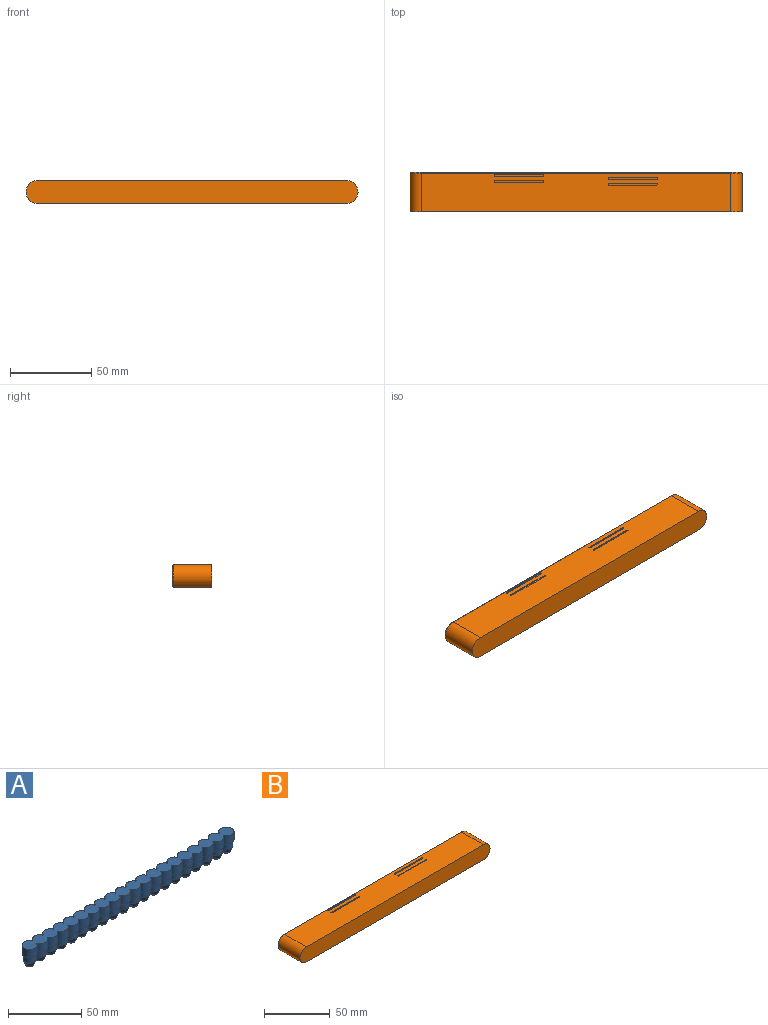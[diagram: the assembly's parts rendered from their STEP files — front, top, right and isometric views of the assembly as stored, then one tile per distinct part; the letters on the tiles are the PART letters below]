
ASSEMBLY  parts=2 mates=1
PART A: 158 faces, bbox 200.4x10.4x17 mm
  f0: cylinder r=5.2mm len=10.4mm, axis (0,0,1), area 198.4mm2, adj f66,f67,f76,f157
  f1: cylinder r=5.2mm len=9.51mm, axis (0,0,1), area 84.1mm2, adj f65,f66,f76,f157
  f2: cylinder r=5.2mm len=9.51mm, axis (0,0,1), area 84.1mm2, adj f64,f65,f76,f157
  f3: cylinder r=5.2mm len=9.51mm, axis (0,0,1), area 84.1mm2, adj f63,f64,f76,f157
  f4: cylinder r=5.2mm len=9.51mm, axis (0,0,1), area 84.1mm2, adj f62,f63,f76,f157
  f5: cylinder r=5.2mm len=9.51mm, axis (0,0,1), area 84.1mm2, adj f61,f62,f76,f157
  f6: cylinder r=5.2mm len=9.51mm, axis (0,0,1), area 84.1mm2, adj f60,f61,f76,f157
  f7: cylinder r=5.2mm len=9.51mm, axis (0,0,1), area 84.1mm2, adj f59,f60,f76,f157
  f8: cylinder r=5.2mm len=9.51mm, axis (0,0,1), area 84.1mm2, adj f58,f59,f76,f157
  f9: cylinder r=5.2mm len=9.51mm, axis (0,0,1), area 84.1mm2, adj f57,f58,f76,f157
  f10: cylinder r=5.2mm len=9.51mm, axis (0,0,1), area 84.1mm2, adj f56,f57,f76,f157
  f11: cylinder r=5.2mm len=9.51mm, axis (0,0,1), area 84.1mm2, adj f55,f56,f76,f157
  f12: cylinder r=5.2mm len=9.51mm, axis (0,0,1), area 84.1mm2, adj f54,f55,f76,f157
  f13: cylinder r=5.2mm len=9.51mm, axis (0,0,1), area 84.1mm2, adj f53,f54,f76,f157
  f14: cylinder r=5.2mm len=9.51mm, axis (0,0,1), area 84.1mm2, adj f52,f53,f76,f157
  f15: cylinder r=5.2mm len=9.51mm, axis (0,0,1), area 84.1mm2, adj f51,f52,f76,f157
  f16: cylinder r=5.2mm len=9.51mm, axis (0,0,1), area 84.1mm2, adj f50,f51,f76,f157
  f17: cylinder r=5.2mm len=9.51mm, axis (0,0,1), area 84.1mm2, adj f49,f50,f76,f157
  f18: cylinder r=5.2mm len=9.51mm, axis (0,0,1), area 84.1mm2, adj f48,f49,f76,f157
  f19: cylinder r=5.2mm len=10.4mm, axis (0,0,1), area 198.4mm2, adj f47,f48,f76,f157
  f20: cylinder r=5.2mm len=9.51mm, axis (0,0,1), area 84.1mm2, adj f39,f75,f76,f157
  f21: cylinder r=5.2mm len=9.51mm, axis (0,0,1), area 84.1mm2, adj f74,f75,f76,f157
  f22: cylinder r=5.2mm len=9.51mm, axis (0,0,1), area 84.1mm2, adj f73,f74,f76,f157
  f23: cylinder r=5.2mm len=9.51mm, axis (0,0,1), area 84.1mm2, adj f72,f73,f76,f157
  f24: cylinder r=5.2mm len=9.51mm, axis (0,0,1), area 84.1mm2, adj f71,f72,f76,f157
  f25: cylinder r=5.2mm len=9.51mm, axis (0,0,1), area 84.1mm2, adj f70,f71,f76,f157
  f26: cylinder r=5.2mm len=9.51mm, axis (0,0,1), area 84.1mm2, adj f69,f70,f76,f157
  f27: cylinder r=5.2mm len=9.51mm, axis (0,0,1), area 84.1mm2, adj f68,f69,f76,f157
  f28: cylinder r=5.2mm len=9.51mm, axis (0,0,1), area 84.1mm2, adj f67,f68,f76,f157
  f29: cylinder r=5.2mm len=9.51mm, axis (0,0,1), area 84.1mm2, adj f46,f47,f76,f157
  f30: cylinder r=5.2mm len=9.51mm, axis (0,0,1), area 84.1mm2, adj f45,f46,f76,f157
  f31: cylinder r=5.2mm len=9.51mm, axis (0,0,1), area 84.1mm2, adj f44,f45,f76,f157
  f32: cylinder r=5.2mm len=9.51mm, axis (0,0,1), area 84.1mm2, adj f43,f44,f76,f157
  f33: cylinder r=5.2mm len=9.51mm, axis (0,0,1), area 84.1mm2, adj f42,f43,f76,f157
  f34: cylinder r=5.2mm len=9.51mm, axis (0,0,1), area 84.1mm2, adj f41,f42,f76,f157
  f35: cylinder r=5.2mm len=9.51mm, axis (0,0,1), area 84.1mm2, adj f40,f41,f76,f157
  f36: cylinder r=5.2mm len=9.51mm, axis (0,0,1), area 84.1mm2, adj f38,f40,f76,f157
  f37: cylinder r=5.2mm len=9.51mm, axis (0,0,1), area 84.1mm2, adj f38,f39,f76,f157
  f38: plane 7x0.49mm, normal (0,-1,0), area 3.4mm2, adj f36,f37,f76,f157
  f39: plane 7x0.49mm, normal (0,-1,0), area 3.4mm2, adj f20,f37,f76,f157
  f40: plane 7x0.49mm, normal (0,-1,0), area 3.4mm2, adj f35,f36,f76,f157
  f41: plane 7x0.49mm, normal (0,-1,0), area 3.4mm2, adj f34,f35,f76,f157
  f42: plane 7x0.49mm, normal (0,-1,0), area 3.4mm2, adj f33,f34,f76,f157
  f43: plane 7x0.49mm, normal (0,-1,0), area 3.4mm2, adj f32,f33,f76,f157
  f44: plane 7x0.49mm, normal (0,-1,0), area 3.4mm2, adj f31,f32,f76,f157
  f45: plane 7x0.49mm, normal (0,-1,0), area 3.4mm2, adj f30,f31,f76,f157
  f46: plane 7x0.49mm, normal (0,-1,0), area 3.4mm2, adj f29,f30,f76,f157
  f47: plane 7x0.49mm, normal (0,-1,0), area 3.4mm2, adj f19,f29,f76,f157
  f48: plane 7x0.49mm, normal (0,1,0), area 3.4mm2, adj f18,f19,f76,f157
  f49: plane 7x0.49mm, normal (0,1,0), area 3.4mm2, adj f17,f18,f76,f157
  f50: plane 7x0.49mm, normal (0,1,0), area 3.4mm2, adj f16,f17,f76,f157
  f51: plane 7x0.49mm, normal (0,1,0), area 3.4mm2, adj f15,f16,f76,f157
  f52: plane 7x0.49mm, normal (0,1,0), area 3.4mm2, adj f14,f15,f76,f157
  f53: plane 7x0.49mm, normal (0,1,0), area 3.4mm2, adj f13,f14,f76,f157
  f54: plane 7x0.49mm, normal (0,1,0), area 3.4mm2, adj f12,f13,f76,f157
  f55: plane 7x0.49mm, normal (0,1,0), area 3.4mm2, adj f11,f12,f76,f157
  f56: plane 7x0.49mm, normal (0,1,0), area 3.4mm2, adj f10,f11,f76,f157
  f57: plane 7x0.49mm, normal (0,1,0), area 3.4mm2, adj f9,f10,f76,f157
  f58: plane 7x0.49mm, normal (0,1,0), area 3.4mm2, adj f8,f9,f76,f157
  f59: plane 7x0.49mm, normal (0,1,0), area 3.4mm2, adj f7,f8,f76,f157
  f60: plane 7x0.49mm, normal (0,1,0), area 3.4mm2, adj f6,f7,f76,f157
  f61: plane 7x0.49mm, normal (0,1,0), area 3.4mm2, adj f5,f6,f76,f157
  f62: plane 7x0.49mm, normal (0,1,0), area 3.4mm2, adj f4,f5,f76,f157
  f63: plane 7x0.49mm, normal (0,1,0), area 3.4mm2, adj f3,f4,f76,f157
  f64: plane 7x0.49mm, normal (0,1,0), area 3.4mm2, adj f2,f3,f76,f157
  f65: plane 7x0.49mm, normal (0,1,0), area 3.4mm2, adj f1,f2,f76,f157
  f66: plane 7x0.49mm, normal (0,1,0), area 3.4mm2, adj f0,f1,f76,f157
  f67: plane 7x0.49mm, normal (0,-1,0), area 3.4mm2, adj f0,f28,f76,f157
  f68: plane 7x0.49mm, normal (0,-1,0), area 3.4mm2, adj f27,f28,f76,f157
  f69: plane 7x0.49mm, normal (0,-1,0), area 3.4mm2, adj f26,f27,f76,f157
  f70: plane 7x0.49mm, normal (0,-1,0), area 3.4mm2, adj f25,f26,f76,f157
  f71: plane 7x0.49mm, normal (0,-1,0), area 3.4mm2, adj f24,f25,f76,f157
  f72: plane 7x0.49mm, normal (0,-1,0), area 3.4mm2, adj f23,f24,f76,f157
  f73: plane 7x0.49mm, normal (0,-1,0), area 3.4mm2, adj f22,f23,f76,f157
  f74: plane 7x0.49mm, normal (0,-1,0), area 3.4mm2, adj f21,f22,f76,f157
  f75: plane 7x0.49mm, normal (0,-1,0), area 3.4mm2, adj f20,f21,f76,f157
  f76: plane 200.4x10.4mm, normal (0,0,-1), area 417.9mm2, adj f0,f1,f2,f3,f4,f5,f6,f7
  f77: cylinder r=4.5mm len=9mm, axis (0,0,1), area 141.4mm2, adj f76,f136
  f78: plane 2.29x2.29mm, normal (0,0,-1), area 4.1mm2, adj f137
  f79: cylinder r=4.5mm len=9mm, axis (0,0,1), area 141.4mm2, adj f76,f135
  f80: plane 2.29x2.29mm, normal (0,0,-1), area 4.1mm2, adj f138
  f81: cylinder r=4.5mm len=9mm, axis (0,0,1), area 141.4mm2, adj f76,f134
  f82: plane 2.29x2.29mm, normal (0,0,-1), area 4.1mm2, adj f139
  f83: cylinder r=4.5mm len=9mm, axis (0,0,1), area 141.4mm2, adj f76,f133
  f84: plane 2.29x2.29mm, normal (0,0,-1), area 4.1mm2, adj f140
  f85: cylinder r=4.5mm len=9mm, axis (0,0,1), area 141.4mm2, adj f76,f132
  f86: plane 2.29x2.29mm, normal (0,0,-1), area 4.1mm2, adj f141
  f87: cylinder r=4.5mm len=9mm, axis (0,0,1), area 141.4mm2, adj f76,f131
  f88: plane 2.29x2.29mm, normal (0,0,-1), area 4.1mm2, adj f142
  f89: cylinder r=4.5mm len=9mm, axis (0,0,1), area 141.4mm2, adj f76,f130
  f90: plane 2.29x2.29mm, normal (0,0,-1), area 4.1mm2, adj f143
  f91: cylinder r=4.5mm len=9mm, axis (0,0,1), area 141.4mm2, adj f76,f129
  f92: plane 2.29x2.29mm, normal (0,0,-1), area 4.1mm2, adj f144
  f93: cylinder r=4.5mm len=9mm, axis (0,0,1), area 141.4mm2, adj f76,f128
  f94: plane 2.29x2.29mm, normal (0,0,-1), area 4.1mm2, adj f145
  f95: cylinder r=4.5mm len=9mm, axis (0,0,1), area 141.4mm2, adj f76,f127
  f96: plane 2.29x2.29mm, normal (0,0,-1), area 4.1mm2, adj f146
  f97: cylinder r=4.5mm len=9mm, axis (0,0,1), area 141.4mm2, adj f76,f126
  f98: plane 2.29x2.29mm, normal (0,0,-1), area 4.1mm2, adj f147
  f99: cylinder r=4.5mm len=9mm, axis (0,0,1), area 141.4mm2, adj f76,f125
  f100: plane 2.29x2.29mm, normal (0,0,-1), area 4.1mm2, adj f148
  f101: cylinder r=4.5mm len=9mm, axis (0,0,1), area 141.4mm2, adj f76,f124
  f102: plane 2.29x2.29mm, normal (0,0,-1), area 4.1mm2, adj f149
  f103: cylinder r=4.5mm len=9mm, axis (0,0,1), area 141.4mm2, adj f76,f123
  f104: plane 2.29x2.29mm, normal (0,0,-1), area 4.1mm2, adj f150
  f105: cylinder r=4.5mm len=9mm, axis (0,0,1), area 141.4mm2, adj f76,f122
  f106: plane 2.29x2.29mm, normal (0,0,-1), area 4.1mm2, adj f151
  f107: cylinder r=4.5mm len=9mm, axis (0,0,1), area 141.4mm2, adj f76,f121
  f108: plane 2.29x2.29mm, normal (0,0,-1), area 4.1mm2, adj f152
  f109: cylinder r=4.5mm len=9mm, axis (0,0,1), area 141.4mm2, adj f76,f120
  f110: plane 2.29x2.29mm, normal (0,0,-1), area 4.1mm2, adj f153
  f111: cylinder r=4.5mm len=9mm, axis (0,0,1), area 141.4mm2, adj f76,f119
  f112: plane 2.29x2.29mm, normal (0,0,-1), area 4.1mm2, adj f154
  f113: cylinder r=4.5mm len=9mm, axis (0,0,1), area 141.4mm2, adj f76,f118
  f114: plane 2.29x2.29mm, normal (0,0,-1), area 4.1mm2, adj f155
  f115: cylinder r=4.5mm len=9mm, axis (0,0,1), area 141.4mm2, adj f76,f117
  f116: plane 2.29x2.29mm, normal (0,0,-1), area 4.1mm2, adj f156
  f117: cone r=2.5mm half-angle=21.8deg, axis (0,0,1), area 95mm2, adj f115,f156
  f118: cone r=2.5mm half-angle=21.8deg, axis (0,0,1), area 95mm2, adj f113,f155
  f119: cone r=2.5mm half-angle=21.8deg, axis (0,0,1), area 95mm2, adj f111,f154
  f120: cone r=2.5mm half-angle=21.8deg, axis (0,0,1), area 95mm2, adj f109,f153
  f121: cone r=2.5mm half-angle=21.8deg, axis (0,0,1), area 95mm2, adj f107,f152
  f122: cone r=2.5mm half-angle=21.8deg, axis (0,0,1), area 95mm2, adj f105,f151
  f123: cone r=2.5mm half-angle=21.8deg, axis (0,0,1), area 95mm2, adj f103,f150
  f124: cone r=2.5mm half-angle=21.8deg, axis (0,0,1), area 95mm2, adj f101,f149
  f125: cone r=2.5mm half-angle=21.8deg, axis (0,0,1), area 95mm2, adj f99,f148
  f126: cone r=2.5mm half-angle=21.8deg, axis (0,0,1), area 95mm2, adj f97,f147
  f127: cone r=2.5mm half-angle=21.8deg, axis (0,0,1), area 95mm2, adj f95,f146
  f128: cone r=2.5mm half-angle=21.8deg, axis (0,0,1), area 95mm2, adj f93,f145
  f129: cone r=2.5mm half-angle=21.8deg, axis (0,0,1), area 95mm2, adj f91,f144
  f130: cone r=2.5mm half-angle=21.8deg, axis (0,0,1), area 95mm2, adj f89,f143
  f131: cone r=2.5mm half-angle=21.8deg, axis (0,0,1), area 95mm2, adj f87,f142
  f132: cone r=2.5mm half-angle=21.8deg, axis (0,0,1), area 95mm2, adj f85,f141
  f133: cone r=2.5mm half-angle=21.8deg, axis (0,0,1), area 95mm2, adj f83,f140
  f134: cone r=2.5mm half-angle=21.8deg, axis (0,0,1), area 95mm2, adj f81,f139
  f135: cone r=2.5mm half-angle=21.8deg, axis (0,0,1), area 95mm2, adj f79,f138
  f136: cone r=2.5mm half-angle=21.8deg, axis (0,0,1), area 95mm2, adj f77,f137
  f137: torus R=1.15mm, axis (0,0,-1), area 32.9mm2, adj f78,f136
  f138: torus R=1.15mm, axis (0,0,-1), area 32.9mm2, adj f80,f135
  f139: torus R=1.15mm, axis (0,0,-1), area 32.9mm2, adj f82,f134
  f140: torus R=1.15mm, axis (0,0,-1), area 32.9mm2, adj f84,f133
  f141: torus R=1.15mm, axis (0,0,-1), area 32.9mm2, adj f86,f132
  f142: torus R=1.15mm, axis (0,0,-1), area 32.9mm2, adj f88,f131
  f143: torus R=1.15mm, axis (0,0,-1), area 32.9mm2, adj f90,f130
  f144: torus R=1.15mm, axis (0,0,-1), area 32.9mm2, adj f92,f129
  f145: torus R=1.15mm, axis (0,0,-1), area 32.9mm2, adj f94,f128
  f146: torus R=1.15mm, axis (0,0,-1), area 32.9mm2, adj f96,f127
  f147: torus R=1.15mm, axis (0,0,-1), area 32.9mm2, adj f98,f126
  f148: torus R=1.15mm, axis (0,0,-1), area 32.9mm2, adj f100,f125
  f149: torus R=1.15mm, axis (0,0,-1), area 32.9mm2, adj f102,f124
  f150: torus R=1.15mm, axis (0,0,-1), area 32.9mm2, adj f104,f123
  f151: torus R=1.15mm, axis (0,0,-1), area 32.9mm2, adj f106,f122
  f152: torus R=1.15mm, axis (0,0,-1), area 32.9mm2, adj f108,f121
  f153: torus R=1.15mm, axis (0,0,-1), area 32.9mm2, adj f110,f120
  f154: torus R=1.15mm, axis (0,0,-1), area 32.9mm2, adj f112,f119
  f155: torus R=1.15mm, axis (0,0,-1), area 32.9mm2, adj f114,f118
  f156: torus R=1.15mm, axis (0,0,-1), area 32.9mm2, adj f116,f117
  f157: plane 200.4x10.4mm, normal (0,0,1), area 1690.2mm2, adj f0,f1,f2,f3,f4,f5,f6,f7
PART B: 187 faces, bbox 204x24x14 mm
  f0: plane 29x0.5mm, normal (0,-1,0), area 14.5mm2, adj f2,f6,f179,f183
  f1: plane 29x0.5mm, normal (0,1,0), area 14.5mm2, adj f2,f6,f179,f183
  f2: plane 30x1mm, normal (0,0,1), area 29.8mm2, adj f0,f1,f179,f183
  f3: plane 29x0.5mm, normal (0,-1,0), area 14.5mm2, adj f5,f6,f181,f185
  f4: plane 29x0.5mm, normal (0,1,0), area 14.5mm2, adj f5,f6,f181,f185
  f5: plane 30x1mm, normal (0,0,1), area 29.8mm2, adj f3,f4,f181,f185
  f6: plane 190x23.5mm, normal (0,0,1), area 4345.9mm2, adj f0,f1,f3,f4,f127,f128,f129,f131
  f7: cylinder r=5.2mm len=10.4mm, axis (0,1,0), area 255.1mm2, adj f27,f46,f170,f171
  f8: cylinder r=5.2mm len=9.51mm, axis (0,1,0), area 108.1mm2, adj f27,f46,f169,f170
  f9: cylinder r=5.2mm len=9.51mm, axis (0,1,0), area 108.1mm2, adj f27,f46,f168,f169
  f10: cylinder r=5.2mm len=9.51mm, axis (0,1,0), area 108.1mm2, adj f27,f46,f167,f168
  f11: cylinder r=5.2mm len=9.51mm, axis (0,1,0), area 108.1mm2, adj f27,f46,f166,f167
  f12: cylinder r=5.2mm len=9.51mm, axis (0,1,0), area 108.1mm2, adj f27,f46,f165,f166
  f13: cylinder r=5.2mm len=9.51mm, axis (0,1,0), area 108.1mm2, adj f27,f46,f164,f165
  f14: cylinder r=5.2mm len=9.51mm, axis (0,1,0), area 108.1mm2, adj f27,f46,f163,f164
  f15: cylinder r=5.2mm len=9.51mm, axis (0,1,0), area 108.1mm2, adj f27,f46,f162,f163
  f16: cylinder r=5.2mm len=9.51mm, axis (0,1,0), area 108.1mm2, adj f27,f46,f161,f162
  f17: cylinder r=5.2mm len=9.51mm, axis (0,1,0), area 108.1mm2, adj f27,f46,f160,f161
  f18: cylinder r=5.2mm len=9.51mm, axis (0,1,0), area 108.1mm2, adj f27,f46,f159,f160
  f19: cylinder r=5.2mm len=9.51mm, axis (0,1,0), area 108.1mm2, adj f27,f46,f158,f159
  f20: cylinder r=5.2mm len=9.51mm, axis (0,1,0), area 108.1mm2, adj f27,f46,f157,f158
  f21: cylinder r=5.2mm len=9.51mm, axis (0,1,0), area 108.1mm2, adj f27,f46,f156,f157
  f22: cylinder r=5.2mm len=9.51mm, axis (0,1,0), area 108.1mm2, adj f27,f46,f155,f156
  f23: cylinder r=5.2mm len=9.51mm, axis (0,1,0), area 108.1mm2, adj f27,f46,f154,f155
  f24: cylinder r=5.2mm len=9.51mm, axis (0,1,0), area 108.1mm2, adj f27,f46,f153,f154
  f25: cylinder r=5.2mm len=9.51mm, axis (0,1,0), area 108.1mm2, adj f27,f46,f152,f153
  f26: cylinder r=5.2mm len=10.4mm, axis (0,1,0), area 255.1mm2, adj f27,f46,f151,f152
  f27: plane 203x13mm, normal (0,1,0), area 912.5mm2, adj f7,f8,f9,f10,f11,f12,f13,f14
  f28: cylinder r=5.2mm len=9.51mm, axis (0,1,0), area 108.1mm2, adj f27,f46,f136,f172
  f29: cylinder r=5.2mm len=9.51mm, axis (0,1,0), area 108.1mm2, adj f27,f46,f171,f172
  f30: cylinder r=5.2mm len=9.51mm, axis (0,1,0), area 108.1mm2, adj f27,f46,f150,f151
  f31: cylinder r=5.2mm len=9.51mm, axis (0,1,0), area 108.1mm2, adj f27,f46,f149,f150
  f32: cylinder r=5.2mm len=9.51mm, axis (0,1,0), area 108.1mm2, adj f27,f46,f148,f149
  f33: cylinder r=5.2mm len=9.51mm, axis (0,1,0), area 108.1mm2, adj f27,f46,f147,f148
  f34: cylinder r=5.2mm len=9.51mm, axis (0,1,0), area 108.1mm2, adj f27,f46,f146,f147
  f35: cylinder r=5.2mm len=9.51mm, axis (0,1,0), area 108.1mm2, adj f27,f46,f145,f146
  f36: cylinder r=5.2mm len=9.51mm, axis (0,1,0), area 108.1mm2, adj f27,f46,f144,f145
  f37: cylinder r=5.2mm len=9.51mm, axis (0,1,0), area 108.1mm2, adj f27,f46,f143,f144
  f38: cylinder r=5.2mm len=9.51mm, axis (0,1,0), area 108.1mm2, adj f27,f46,f142,f143
  f39: cylinder r=5.2mm len=9.51mm, axis (0,1,0), area 108.1mm2, adj f27,f46,f141,f142
  f40: cylinder r=5.2mm len=9.51mm, axis (0,1,0), area 108.1mm2, adj f27,f46,f140,f141
  f41: cylinder r=5.2mm len=9.51mm, axis (0,1,0), area 108.1mm2, adj f27,f46,f139,f140
  f42: cylinder r=5.2mm len=9.51mm, axis (0,1,0), area 108.1mm2, adj f27,f46,f138,f139
  f43: cylinder r=5.2mm len=9.51mm, axis (0,1,0), area 108.1mm2, adj f27,f46,f137,f138
  f44: cylinder r=5.2mm len=9.51mm, axis (0,1,0), area 108.1mm2, adj f27,f46,f135,f137
  f45: cylinder r=5.2mm len=9.51mm, axis (0,1,0), area 108.1mm2, adj f27,f46,f135,f136
  f46: plane 200.4x10.4mm, normal (0,1,0), area 417.9mm2, adj f7,f8,f9,f10,f11,f12,f13,f14
  f47: cylinder r=4.5mm len=9mm, axis (0,1,0), area 141.4mm2, adj f46,f87
  f48: plane 2.29x2.29mm, normal (0,1,0), area 4.1mm2, adj f126
  f49: cylinder r=4.5mm len=9mm, axis (0,1,0), area 141.4mm2, adj f46,f88
  f50: plane 2.29x2.29mm, normal (0,1,0), area 4.1mm2, adj f125
  f51: cylinder r=4.5mm len=9mm, axis (0,1,0), area 141.4mm2, adj f46,f89
  f52: plane 2.29x2.29mm, normal (0,1,0), area 4.1mm2, adj f124
  f53: cylinder r=4.5mm len=9mm, axis (0,1,0), area 141.4mm2, adj f46,f90
  f54: plane 2.29x2.29mm, normal (0,1,0), area 4.1mm2, adj f123
  f55: cylinder r=4.5mm len=9mm, axis (0,1,0), area 141.4mm2, adj f46,f91
  f56: plane 2.29x2.29mm, normal (0,1,0), area 4.1mm2, adj f122
  f57: cylinder r=4.5mm len=9mm, axis (0,1,0), area 141.4mm2, adj f46,f92
  f58: plane 2.29x2.29mm, normal (0,1,0), area 4.1mm2, adj f121
  f59: cylinder r=4.5mm len=9mm, axis (0,1,0), area 141.4mm2, adj f46,f93
  f60: plane 2.29x2.29mm, normal (0,1,0), area 4.1mm2, adj f120
  f61: cylinder r=4.5mm len=9mm, axis (0,1,0), area 141.4mm2, adj f46,f94
  f62: plane 2.29x2.29mm, normal (0,1,0), area 4.1mm2, adj f119
  f63: cylinder r=4.5mm len=9mm, axis (0,1,0), area 141.4mm2, adj f46,f95
  f64: plane 2.29x2.29mm, normal (0,1,0), area 4.1mm2, adj f118
  f65: cylinder r=4.5mm len=9mm, axis (0,1,0), area 141.4mm2, adj f46,f96
  f66: plane 2.29x2.29mm, normal (0,1,0), area 4.1mm2, adj f117
  f67: cylinder r=4.5mm len=9mm, axis (0,1,0), area 141.4mm2, adj f46,f97
  f68: plane 2.29x2.29mm, normal (0,1,0), area 4.1mm2, adj f116
  f69: cylinder r=4.5mm len=9mm, axis (0,1,0), area 141.4mm2, adj f46,f98
  f70: plane 2.29x2.29mm, normal (0,1,0), area 4.1mm2, adj f115
  f71: cylinder r=4.5mm len=9mm, axis (0,1,0), area 141.4mm2, adj f46,f99
  f72: plane 2.29x2.29mm, normal (0,1,0), area 4.1mm2, adj f114
  f73: cylinder r=4.5mm len=9mm, axis (0,1,0), area 141.4mm2, adj f46,f100
  f74: plane 2.29x2.29mm, normal (0,1,0), area 4.1mm2, adj f113
  f75: cylinder r=4.5mm len=9mm, axis (0,1,0), area 141.4mm2, adj f46,f101
  f76: plane 2.29x2.29mm, normal (0,1,0), area 4.1mm2, adj f112
  f77: cylinder r=4.5mm len=9mm, axis (0,1,0), area 141.4mm2, adj f46,f102
  f78: plane 2.29x2.29mm, normal (0,1,0), area 4.1mm2, adj f111
  f79: cylinder r=4.5mm len=9mm, axis (0,1,0), area 141.4mm2, adj f46,f103
  f80: plane 2.29x2.29mm, normal (0,1,0), area 4.1mm2, adj f110
  f81: cylinder r=4.5mm len=9mm, axis (0,1,0), area 141.4mm2, adj f46,f104
  f82: plane 2.29x2.29mm, normal (0,1,0), area 4.1mm2, adj f109
  f83: cylinder r=4.5mm len=9mm, axis (0,1,0), area 141.4mm2, adj f46,f105
  f84: plane 2.29x2.29mm, normal (0,1,0), area 4.1mm2, adj f108
  f85: cylinder r=4.5mm len=9mm, axis (0,1,0), area 141.4mm2, adj f46,f106
  f86: plane 2.29x2.29mm, normal (0,1,0), area 4.1mm2, adj f107
  f87: cone r=2.5mm half-angle=21.8deg, axis (0,1,0), area 95mm2, adj f47,f126
  f88: cone r=2.5mm half-angle=21.8deg, axis (0,1,0), area 95mm2, adj f49,f125
  f89: cone r=2.5mm half-angle=21.8deg, axis (0,1,0), area 95mm2, adj f51,f124
  f90: cone r=2.5mm half-angle=21.8deg, axis (0,1,0), area 95mm2, adj f53,f123
  f91: cone r=2.5mm half-angle=21.8deg, axis (0,1,0), area 95mm2, adj f55,f122
  f92: cone r=2.5mm half-angle=21.8deg, axis (0,1,0), area 95mm2, adj f57,f121
  f93: cone r=2.5mm half-angle=21.8deg, axis (0,1,0), area 95mm2, adj f59,f120
  f94: cone r=2.5mm half-angle=21.8deg, axis (0,1,0), area 95mm2, adj f61,f119
  f95: cone r=2.5mm half-angle=21.8deg, axis (0,1,0), area 95mm2, adj f63,f118
  f96: cone r=2.5mm half-angle=21.8deg, axis (0,1,0), area 95mm2, adj f65,f117
  f97: cone r=2.5mm half-angle=21.8deg, axis (0,1,0), area 95mm2, adj f67,f116
  f98: cone r=2.5mm half-angle=21.8deg, axis (0,1,0), area 95mm2, adj f69,f115
  f99: cone r=2.5mm half-angle=21.8deg, axis (0,1,0), area 95mm2, adj f71,f114
  f100: cone r=2.5mm half-angle=21.8deg, axis (0,1,0), area 95mm2, adj f73,f113
  f101: cone r=2.5mm half-angle=21.8deg, axis (0,1,0), area 95mm2, adj f75,f112
  f102: cone r=2.5mm half-angle=21.8deg, axis (0,1,0), area 95mm2, adj f77,f111
  f103: cone r=2.5mm half-angle=21.8deg, axis (0,1,0), area 95mm2, adj f79,f110
  f104: cone r=2.5mm half-angle=21.8deg, axis (0,1,0), area 95mm2, adj f81,f109
  f105: cone r=2.5mm half-angle=21.8deg, axis (0,1,0), area 95mm2, adj f83,f108
  f106: cone r=2.5mm half-angle=21.8deg, axis (0,1,0), area 95mm2, adj f85,f107
  f107: torus R=1.15mm, axis (0,1,0), area 32.9mm2, adj f86,f106
  f108: torus R=1.15mm, axis (0,1,0), area 32.9mm2, adj f84,f105
  f109: torus R=1.15mm, axis (0,1,0), area 32.9mm2, adj f82,f104
  f110: torus R=1.15mm, axis (0,1,0), area 32.9mm2, adj f80,f103
  f111: torus R=1.15mm, axis (0,1,0), area 32.9mm2, adj f78,f102
  f112: torus R=1.15mm, axis (0,1,0), area 32.9mm2, adj f76,f101
  f113: torus R=1.15mm, axis (0,1,0), area 32.9mm2, adj f74,f100
  f114: torus R=1.15mm, axis (0,1,0), area 32.9mm2, adj f72,f99
  f115: torus R=1.15mm, axis (0,1,0), area 32.9mm2, adj f70,f98
  f116: torus R=1.15mm, axis (0,1,0), area 32.9mm2, adj f68,f97
  f117: torus R=1.15mm, axis (0,1,0), area 32.9mm2, adj f66,f96
  f118: torus R=1.15mm, axis (0,1,0), area 32.9mm2, adj f64,f95
  f119: torus R=1.15mm, axis (0,1,0), area 32.9mm2, adj f62,f94
  f120: torus R=1.15mm, axis (0,1,0), area 32.9mm2, adj f60,f93
  f121: torus R=1.15mm, axis (0,1,0), area 32.9mm2, adj f58,f92
  f122: torus R=1.15mm, axis (0,1,0), area 32.9mm2, adj f56,f91
  f123: torus R=1.15mm, axis (0,1,0), area 32.9mm2, adj f54,f90
  f124: torus R=1.15mm, axis (0,1,0), area 32.9mm2, adj f52,f89
  f125: torus R=1.15mm, axis (0,1,0), area 32.9mm2, adj f50,f88
  f126: torus R=1.15mm, axis (0,1,0), area 32.9mm2, adj f48,f87
  f127: plane 204x14mm, normal (0,-1,0), area 2813.9mm2, adj f6,f128,f129,f130
  f128: cylinder r=7mm len=23.5mm, axis (0,-1,0), area 516.8mm2, adj f6,f127,f130,f133
  f129: cylinder r=7mm len=23.5mm, axis (0,1,0), area 516.8mm2, adj f6,f127,f130,f132
  f130: plane 190x23.5mm, normal (0,0,-1), area 4465mm2, adj f127,f128,f129,f134
  f131: plane 190x0.5mm, normal (0,0.71,0.71), area 134.4mm2, adj f6,f27,f132,f133
  f132: cone r=6.5mm half-angle=45deg, axis (0,-1,0), area 15mm2, adj f27,f129,f131,f134
  f133: cone r=6.5mm half-angle=45deg, axis (0,-1,0), area 15mm2, adj f27,f128,f131,f134
  f134: plane 190x0.5mm, normal (0,0.71,-0.71), area 134.4mm2, adj f27,f130,f132,f133
  f135: plane 9x0.49mm, normal (0,0,1), area 4.4mm2, adj f27,f44,f45,f46
  f136: plane 9x0.49mm, normal (0,0,1), area 4.4mm2, adj f27,f28,f45,f46
  f137: plane 9x0.49mm, normal (0,0,1), area 4.4mm2, adj f27,f43,f44,f46
  f138: plane 9x0.49mm, normal (0,0,1), area 4.4mm2, adj f27,f42,f43,f46
  f139: plane 9x0.49mm, normal (0,0,1), area 4.4mm2, adj f27,f41,f42,f46
  f140: plane 9x0.49mm, normal (0,0,1), area 4.4mm2, adj f27,f40,f41,f46
  f141: plane 9x0.49mm, normal (0,0,1), area 4.4mm2, adj f27,f39,f40,f46
  f142: plane 9x0.49mm, normal (0,0,1), area 4.4mm2, adj f27,f38,f39,f46
  f143: plane 9x0.49mm, normal (0,0,1), area 4.4mm2, adj f27,f37,f38,f46
  f144: plane 9x0.49mm, normal (0,0,1), area 4.4mm2, adj f27,f36,f37,f46
  f145: plane 9x0.49mm, normal (0,0,1), area 4.4mm2, adj f27,f35,f36,f46
  f146: plane 9x0.49mm, normal (0,0,1), area 4.4mm2, adj f27,f34,f35,f46
  f147: plane 9x0.49mm, normal (0,0,1), area 4.4mm2, adj f27,f33,f34,f46
  f148: plane 9x0.49mm, normal (0,0,1), area 4.4mm2, adj f27,f32,f33,f46
  f149: plane 9x0.49mm, normal (0,0,1), area 4.4mm2, adj f27,f31,f32,f46
  f150: plane 9x0.49mm, normal (0,0,1), area 4.4mm2, adj f27,f30,f31,f46
  f151: plane 9x0.49mm, normal (0,0,1), area 4.4mm2, adj f26,f27,f30,f46
  f152: plane 9x0.49mm, normal (0,0,-1), area 4.4mm2, adj f25,f26,f27,f46
  f153: plane 9x0.49mm, normal (0,0,-1), area 4.4mm2, adj f24,f25,f27,f46
  f154: plane 9x0.49mm, normal (0,0,-1), area 4.4mm2, adj f23,f24,f27,f46
  f155: plane 9x0.49mm, normal (0,0,-1), area 4.4mm2, adj f22,f23,f27,f46
  f156: plane 9x0.49mm, normal (0,0,-1), area 4.4mm2, adj f21,f22,f27,f46
  f157: plane 9x0.49mm, normal (0,0,-1), area 4.4mm2, adj f20,f21,f27,f46
  f158: plane 9x0.49mm, normal (0,0,-1), area 4.4mm2, adj f19,f20,f27,f46
  f159: plane 9x0.49mm, normal (0,0,-1), area 4.4mm2, adj f18,f19,f27,f46
  f160: plane 9x0.49mm, normal (0,0,-1), area 4.4mm2, adj f17,f18,f27,f46
  f161: plane 9x0.49mm, normal (0,0,-1), area 4.4mm2, adj f16,f17,f27,f46
  f162: plane 9x0.49mm, normal (0,0,-1), area 4.4mm2, adj f15,f16,f27,f46
  f163: plane 9x0.49mm, normal (0,0,-1), area 4.4mm2, adj f14,f15,f27,f46
  f164: plane 9x0.49mm, normal (0,0,-1), area 4.4mm2, adj f13,f14,f27,f46
  f165: plane 9x0.49mm, normal (0,0,-1), area 4.4mm2, adj f12,f13,f27,f46
  f166: plane 9x0.49mm, normal (0,0,-1), area 4.4mm2, adj f11,f12,f27,f46
  f167: plane 9x0.49mm, normal (0,0,-1), area 4.4mm2, adj f10,f11,f27,f46
  f168: plane 9x0.49mm, normal (0,0,-1), area 4.4mm2, adj f9,f10,f27,f46
  f169: plane 9x0.49mm, normal (0,0,-1), area 4.4mm2, adj f8,f9,f27,f46
  f170: plane 9x0.49mm, normal (0,0,-1), area 4.4mm2, adj f7,f8,f27,f46
  f171: plane 9x0.49mm, normal (0,0,1), area 4.4mm2, adj f7,f27,f29,f46
  f172: plane 9x0.49mm, normal (0,0,1), area 4.4mm2, adj f27,f28,f29,f46
  f173: plane 29x0.5mm, normal (0,-1,0), area 14.5mm2, adj f6,f175,f180,f184
  f174: plane 29x0.5mm, normal (0,1,0), area 14.5mm2, adj f6,f175,f180,f184
  f175: plane 30x1mm, normal (0,0,1), area 29.8mm2, adj f173,f174,f180,f184
  f176: plane 29x0.5mm, normal (0,-1,0), area 14.5mm2, adj f6,f178,f182,f186
  f177: plane 29x0.5mm, normal (0,1,0), area 14.5mm2, adj f6,f178,f182,f186
  f178: plane 30x1mm, normal (0,0,1), area 29.8mm2, adj f176,f177,f182,f186
  f179: cylinder r=0.5mm len=1mm, axis (0,0,1), area 0.8mm2, adj f0,f1,f2,f6
  f180: cylinder r=0.5mm len=1mm, axis (0,0,1), area 0.8mm2, adj f6,f173,f174,f175
  f181: cylinder r=0.5mm len=1mm, axis (0,0,-1), area 0.8mm2, adj f3,f4,f5,f6
  f182: cylinder r=0.5mm len=1mm, axis (0,0,1), area 0.8mm2, adj f6,f176,f177,f178
  f183: cylinder r=0.5mm len=1mm, axis (0,0,-1), area 0.8mm2, adj f0,f1,f2,f6
  f184: cylinder r=0.5mm len=1mm, axis (0,0,1), area 0.8mm2, adj f6,f173,f174,f175
  f185: cylinder r=0.5mm len=1mm, axis (0,0,1), area 0.8mm2, adj f3,f4,f5,f6
  f186: cylinder r=0.5mm len=1mm, axis (0,0,1), area 0.8mm2, adj f6,f176,f177,f178
PLACE A rot(axis=(-1,0,0),90deg) t=(-18.69,-12.81,-24.03)mm
PLACE B t=(-18.69,-8.81,-24.03)mm
MATE fastened A.f19 <-> B.f7  axis (0,1,0) through (-113.69,-14.81,-24.03)mm
